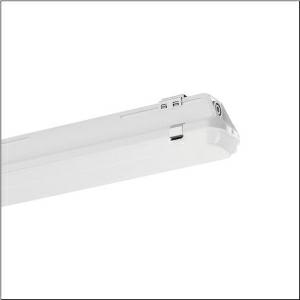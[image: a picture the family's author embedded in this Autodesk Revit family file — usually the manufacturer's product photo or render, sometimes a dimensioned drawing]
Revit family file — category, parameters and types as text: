
# Revit family: monsun_r__11_51fp10dp4b0u007_a74f
name_source: partatom
category: Lighting Fixtures
units: mm (PartAtom-declared; Revit-internal decimal feet)

## family parameters
Cut with Voids When Loaded = No
Host = Face
Light Source = No
Part Type = Normal
Room Calculation Point = No
Round Connector Dimension = Use Diameter
Shared = No

## types (1)
- --- (1 x LED, 12110 lm, 63.7 W, 4000K)
    Apparent Load = 64 VA
    CIE Flux Codes = 47 76 93 94 100
    Color Rendering = 80
    Color Temperature = 4000K
    Default Elevation = 1800 mm
    Description = Monsun® 11, damp-proof luminaire, chain hanger, primary optical cover: enclosure, of PMMA, light emission: direct distribution, primary light characteristic: symmetric, installation type: suspended mounting, surface-mounted, horizontal mounting, vertical mounting, LED, rated luminous flux: 12.110lm, luminous efficacy: 190lm/W, light colour: 840, colour temperature: 4000K, control gear: DALI 2, with terminal, 5-pole, max. 2.5mm², through-wiring: 7x 2.5mm², mains connection: 220..240V, AC, 50/60Hz, rated input power: 64W, housing, of glass-fibre reinforced polyester, uncoated, bright grey, incl. chain hanger, length: 1.590mm, width: 90mm, height: 88mm, clip for enclosure, of stainless steel (V2A), ceiling mounting element, of stainless steel (V2A), chain hanger, of stainless steel (V2A), protection rating (complete): IP66, insulation class (complete): insulation class I (protective earthing), certification: CE, ENEC, VDE, UKCA, protection symbol: D, impact resistance: IK04, permissible operating ambient temperature: -40..+35°C, standard: EN 50419, EN 60598-2-1, corresponds to IFS (International Featured Standards) requirements for safety and quality in the food industry, for indoor or canopied outdoor use, no direct snow, no direct sun, no direct rain, LABS conformity tested according to VDMA 24364:2018-05, contact your sales advisor before using the luminaires in applications with unclear chemical exposure, large temperature fluctuations or condensation-forming humidity, packaging unit: 1 piece
    Height = 89 mm
    Lamp = 1 x LED
    Lamp Light Flux = 12110 lm
    Lamp Power = 63.7 W
    Lamp count = 1
    Length = 1590 mm
    Luminous efficacy = 190 lm/W
    Manufacturer = Siteco
    ModVariant = No
    Model = 51FP10DP4B0U007
    Mounting Place = Ceiling
    Mounting Type = Surface mounted
    Number of Poles = 1
    OnlyDefault = Yes
    Power Factor = 1
    Product Name = Monsun® 11
    Product group = damp-proof luminaire
    ProductGroupID = 301
    Protection Class = Protection class I
    Protection Degree = IP 66
    RLX_Detail_Level = 1
    RLX_Emergency_Light_Flux = 0 lm
    RLX_Emergency_Type = 0
    RLX_Emergency_Type_DB = No
    RlxData = <blob elided: 92389 chars, md5=b1e91e68>
    Socket = socket
    Standby Power = 0 W
    System Light Flux = 12110 lm
    System Power = 64 W
    Type Comments = factory setting: luminous flux: 100 % | dim-lin: 254 | 441 mA
    Type Image = l_1349237.jpg
    URL = http://relux.com
    VarID = @adj_043117
    Voltage = 0 V
    Weight = 0.00 kg
    Width = 90 mm

## geometry (parser evidence)
native form markers: Blend x4, Sweep x14
no freeform markers — native parametric forms only
